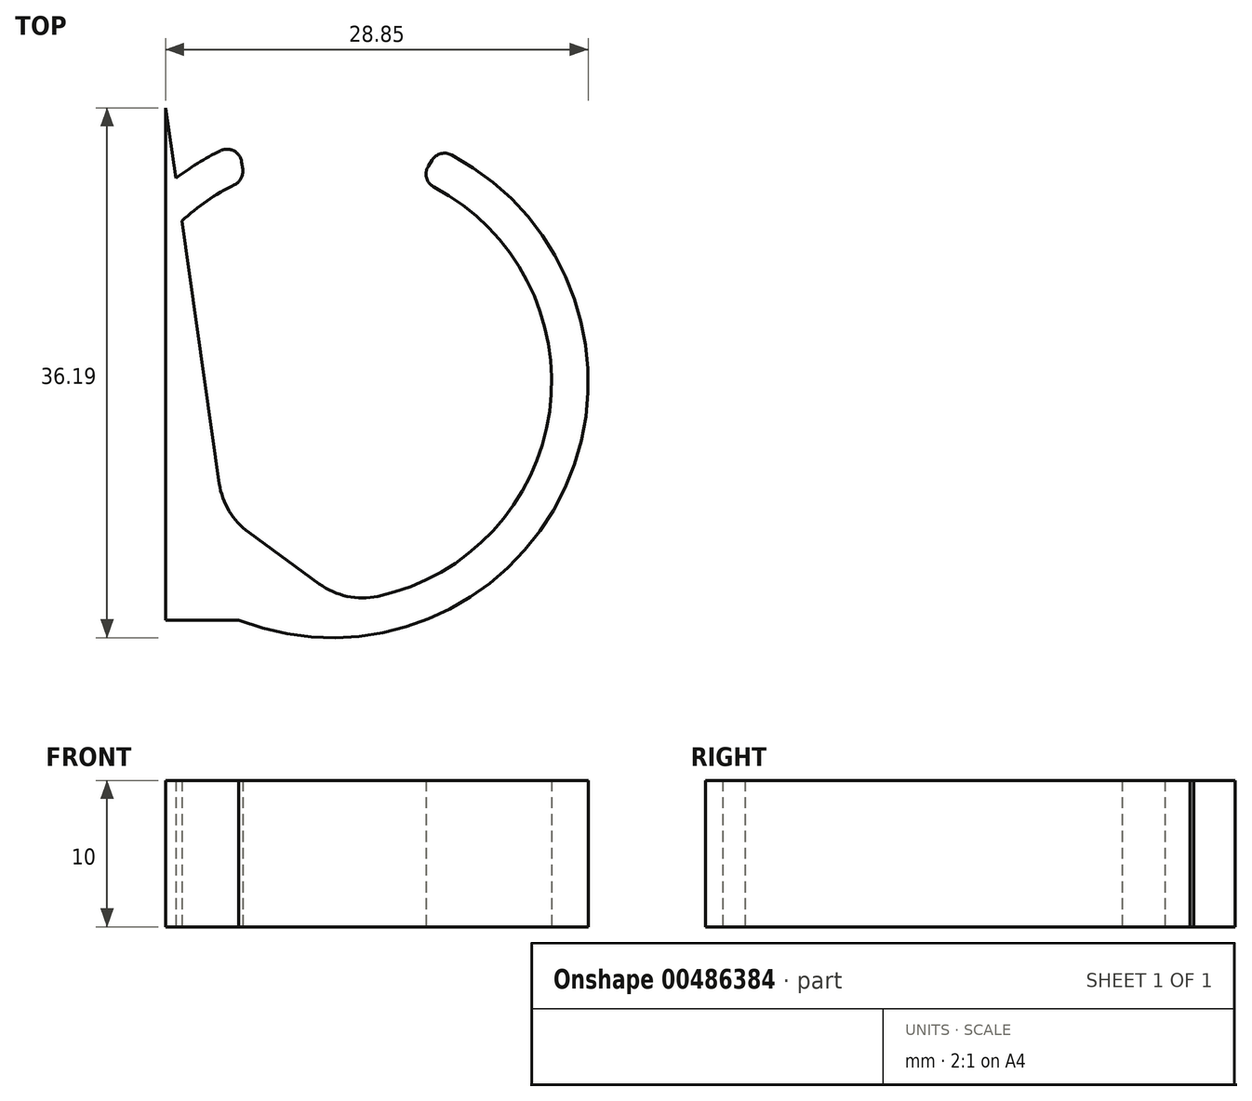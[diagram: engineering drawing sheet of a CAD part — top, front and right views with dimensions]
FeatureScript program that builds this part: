
annotation { "Feature Type Name" : "Feature", "Feature Type Description" : "" }
export const myFeature = defineFeature(function(context is Context, id is Id, definition is map)
    precondition{}
    {
        {
            var Q0;
            Q0=qCreatedBy(makeId("Top.planeOp"),FACE);
            var sketch = newSketch(context, id + "F0", { "sketchPlane" : qUnion([Q0])});
            skLineSegment(sketch, "E0", {"start": v(0, 0) * mm, "end": v(0, 35) * mm});
            skLineSegment(sketch, "E1", {"start": v(0, 0) * mm, "end": v(5, 0) * mm});
            skLineSegment(sketch, "E2", {"start": v(3.67, 9.33) * mm, "end": v(1.1, 27.26) * mm});
            skArc(sketch, "E3", {"start": v(3.76, 32.08) * mm, "mid": v(2.18, 31.21) * mm, "end": v(0.69, 30.18) * mm});
            skPoint(sketch, "E3.second.point", {"position": v(5, 32.61) * mm});
            skPoint(sketch, "E3.third.point", {"position": v(18.68, 32.2) * mm});
            skArc(sketch, "E4", {"start": v(4.71, 29.76) * mm, "mid": v(2.82, 28.64) * mm, "end": v(1.1, 27.26) * mm});
            skLineSegment(sketch, "E5", {"start": v(5.19, 31.32) * mm, "end": v(5.26, 30.8) * mm});
            skLineSegment(sketch, "E6", {"start": v(18.2, 31.44) * mm, "end": v(17.94, 31.01) * mm});
            skArc(sketch, "E7.trimOffspring", {"start": v(5, 0) * mm, "mid": v(27.27, 9.04) * mm, "end": v(19.52, 31.79) * mm});
            skLineSegment(sketch, "E8.trimOffspring", {"start": v(0.69, 30.18) * mm, "end": v(0, 35) * mm});
            skArc(sketch, "E9.trimOffspring", {"start": v(14.48, 1.64) * mm, "mid": v(26.21, 14.27) * mm, "end": v(18.32, 29.6) * mm});
            skLineSegment(sketch, "E10", {"start": v(5.67, 6) * mm, "end": v(10.5, 2.49) * mm});
            skArc(sketch, "E11.filletArc", {"start": v(3.67, 9.33) * mm, "mid": v(4.33, 7.47) * mm, "end": v(5.67, 6) * mm});
            skArc(sketch, "E12.filletArc", {"start": v(10.5, 2.49) * mm, "mid": v(12.4, 1.64) * mm, "end": v(14.48, 1.64) * mm});
            skArc(sketch, "E13.filletArc", {"start": v(5.19, 31.32) * mm, "mid": v(4.67, 32.06) * mm, "end": v(3.76, 32.08) * mm});
            skPoint(sketch, "E14.visualSharp", {"position": v(5.36, 30.06) * mm});
            skArc(sketch, "E14.filletArc", {"start": v(4.71, 29.76) * mm, "mid": v(5.15, 30.19) * mm, "end": v(5.26, 30.8) * mm});
            skArc(sketch, "E15.filletArc", {"start": v(19.52, 31.79) * mm, "mid": v(18.8, 31.87) * mm, "end": v(18.2, 31.44) * mm});
            skPoint(sketch, "E16.visualSharp", {"position": v(17.33, 30.06) * mm});
            skArc(sketch, "E16.filletArc", {"start": v(17.94, 31.01) * mm, "mid": v(17.81, 30.22) * mm, "end": v(18.32, 29.6) * mm});
            skSolve(sketch);
        }
        {
            var Q0;
            Q0=makeQuery(id+"F0.imprint","IMPRINT",FACE,{"disambiguationData":[TD([[makeQuery(id+"F0.imprint","IMPRINT",EDGE,{"derivedFrom":sQuery(id+"F0.wireOp",EDGE,"E0")}),-1.0]])]});
            extrude(context, id + "F1", {"entities" : qUnion([Q0]), "depth" : 10 * mm});
        }
    });
